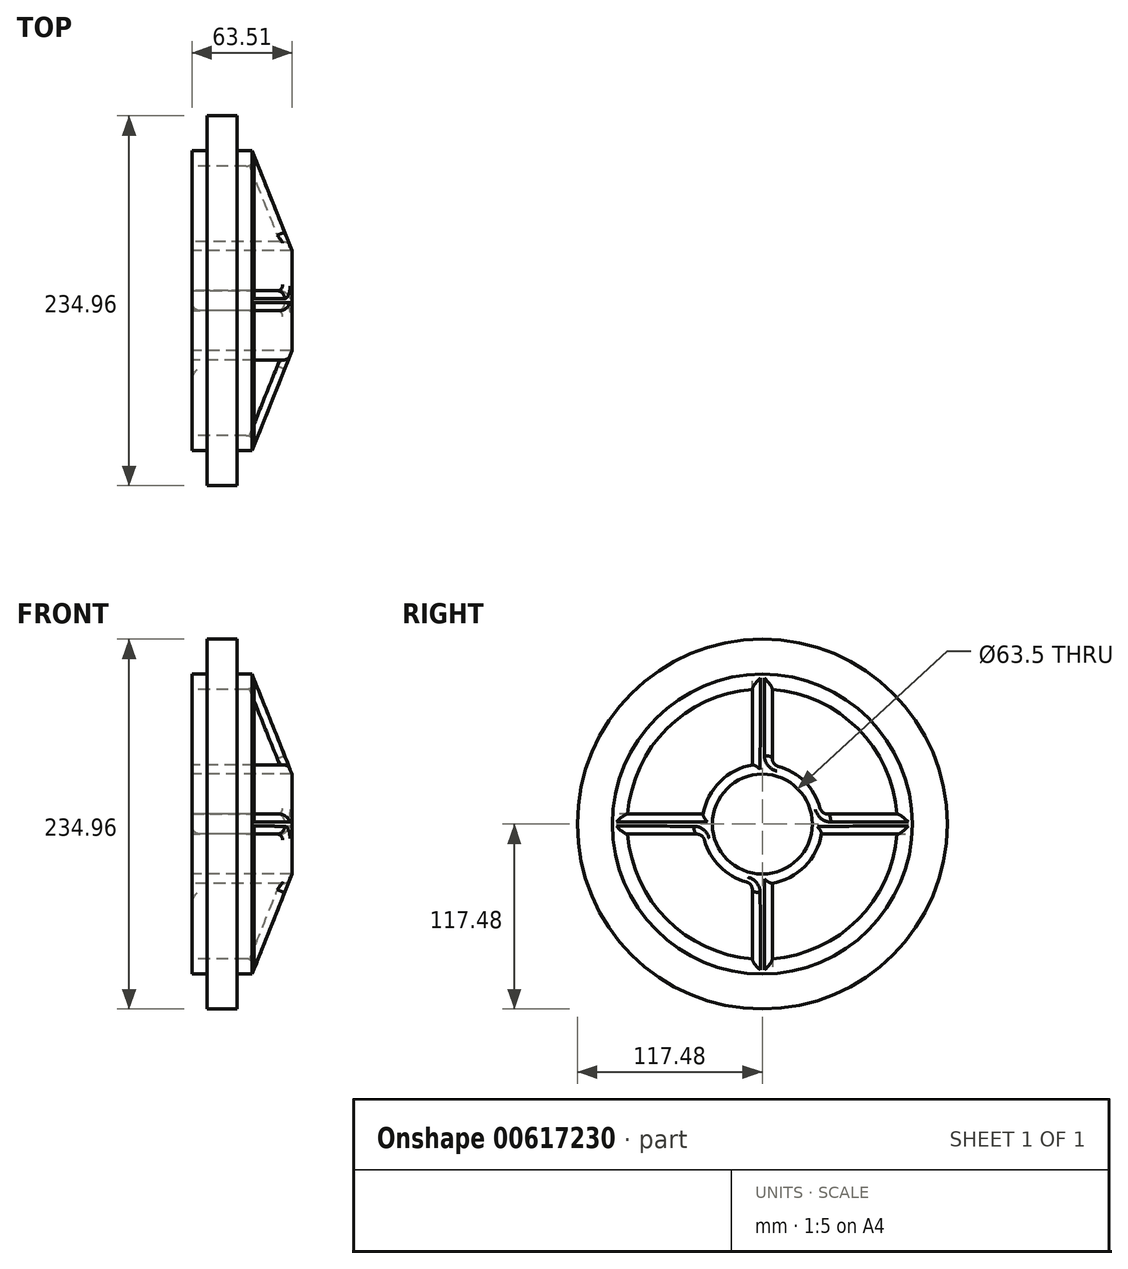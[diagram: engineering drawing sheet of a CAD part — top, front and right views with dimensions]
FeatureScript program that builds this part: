
annotation { "Feature Type Name" : "Feature", "Feature Type Description" : "" }
export const myFeature = defineFeature(function(context is Context, id is Id, definition is map)
    precondition{}
    {
        {
            var Q0;
            Q0=qCreatedBy(makeId("Front.planeOp"),FACE);
            var sketch = newSketch(context, id + "F0", { "sketchPlane" : qUnion([Q0])});
            skLineSegment(sketch, "E0", {"start": v(0, 117.48) * mm, "end": v(19.05, 117.48) * mm});
            skLineSegment(sketch, "E1", {"start": v(19.05, 117.48) * mm, "end": v(19.05, 31.75) * mm});
            skLineSegment(sketch, "E2.bottom", {"start": v(0, 0) * mm, "end": v(0, 0) * mm});
            skLineSegment(sketch, "E2.top", {"start": v(0, 6.04) * mm, "end": v(0, 6.04) * mm});
            skLineSegment(sketch, "E3.top", {"start": v(0, 95.25) * mm, "end": v(-9.53, 95.25) * mm});
            skLineSegment(sketch, "E3.right", {"start": v(-9.52, 31.75) * mm, "end": v(-9.53, 95.25) * mm});
            skLineSegment(sketch, "E4", {"start": v(-9.52, 31.75) * mm, "end": v(53.97, 31.75) * mm});
            skLineSegment(sketch, "E5", {"start": v(19.05, 95.25) * mm, "end": v(28.58, 95.25) * mm});
            skLineSegment(sketch, "E6", {"start": v(-9.53, 31.75) * mm, "end": v(53.97, 31.75) * mm});
            skLineSegment(sketch, "E7", {"start": v(53.97, 31.75) * mm, "end": v(28.57, 95.25) * mm});
            skPoint(sketch, "E8.orphan", {"position": v(19.05, 0) * mm});
            skLineSegment(sketch, "E9.trimOffspring", {"start": v(0, 31.75) * mm, "end": v(0, 95.25) * mm});
            skLineSegment(sketch, "E10.trimOffspring", {"start": v(0, 31.75) * mm, "end": v(0, 117.48) * mm});
            skPoint(sketch, "E11.end.orphan", {"position": v(9.52, 95.25) * mm});
            skPoint(sketch, "E12.start.orphan", {"position": v(-38.35, 0) * mm});
            skLineSegment(sketch, "E13", {"start": v(-18.78, 0) * mm, "end": v(42.61, 0) * mm});
            skSolve(sketch);
        }
        {
            var Q0;
            Q0 = qSketchRegion(id + "F0", true);
            var Q1;
            Q1=sQuery(id+"F0.wireOp",EDGE,"E13");
            revolve(context, id + "F1", {"entities" : qUnion([Q0]), "axis" : qUnion([Q1]), "revolveType" : RevolveType.FULL});
        }
        {
            var Q0;
            Q0=makeQuery(id+"F1.opRevolve","SWEPT_FACE",FACE,{"disambiguationData":[OSD([sQuery(id+"F0.wireOp",EDGE,"E3.right")])]});
            var sketch = newSketch(context, id + "F2", { "sketchPlane" : qUnion([Q0])});
            skLineSegment(sketch, "E14.left", {"start": v(6.35, 85.49) * mm, "end": v(6.35, 37.57) * mm});
            skLineSegment(sketch, "E14.right", {"start": v(-6.35, 85.49) * mm, "end": v(-6.35, 37.57) * mm});
            skLineSegment(sketch, "E15.bottom", {"start": v(85.49, 6.35) * mm, "end": v(37.57, 6.35) * mm});
            skLineSegment(sketch, "E15.top", {"start": v(85.49, -6.35) * mm, "end": v(37.57, -6.35) * mm});
            skArc(sketch, "E16", {"start": v(-6.35, 37.57) * mm, "mid": v(-26.94, 26.94) * mm, "end": v(-37.57, 6.35) * mm});
            skArc(sketch, "E17", {"start": v(-85.49, -6.35) * mm, "mid": v(-60.62, -60.62) * mm, "end": v(-6.35, -85.49) * mm});
            skPoint(sketch, "E18.orphan", {"position": v(-95.04, 6.35) * mm});
            skPoint(sketch, "E19.orphan", {"position": v(-95.04, -6.35) * mm});
            skArc(sketch, "E20.trimOffspring", {"start": v(6.35, -85.49) * mm, "mid": v(60.62, -60.62) * mm, "end": v(85.49, -6.35) * mm});
            skArc(sketch, "E21.trimOffspring", {"start": v(85.49, 6.35) * mm, "mid": v(60.62, 60.62) * mm, "end": v(6.35, 85.49) * mm});
            skPoint(sketch, "E15.left.end.orphan", {"position": v(95.04, -6.35) * mm});
            skPoint(sketch, "E15.left.start.orphan", {"position": v(95.04, 6.35) * mm});
            skPoint(sketch, "E14.top.end.orphan", {"position": v(-6.35, -95.04) * mm});
            skPoint(sketch, "E14.top.start.orphan", {"position": v(6.35, -95.04) * mm});
            skPoint(sketch, "E22.orphan", {"position": v(-6.35, 95.04) * mm});
            skPoint(sketch, "E23.orphan", {"position": v(6.35, 95.04) * mm});
            skArc(sketch, "E24.trimOffspring", {"start": v(-6.35, 85.49) * mm, "mid": v(-60.62, 60.62) * mm, "end": v(-85.49, 6.35) * mm});
            skLineSegment(sketch, "E25.trimOffspring", {"start": v(-37.57, -6.35) * mm, "end": v(-85.49, -6.35) * mm});
            skLineSegment(sketch, "E26.trimOffspring", {"start": v(-37.57, 6.35) * mm, "end": v(-85.49, 6.35) * mm});
            skLineSegment(sketch, "E27.trimOffspring", {"start": v(6.35, -37.57) * mm, "end": v(6.35, -85.49) * mm});
            skLineSegment(sketch, "E28.trimOffspring", {"start": v(-6.35, -37.57) * mm, "end": v(-6.35, -85.49) * mm});
            skArc(sketch, "E29.trimOffspring", {"start": v(-37.57, -6.35) * mm, "mid": v(-26.94, -26.94) * mm, "end": v(-6.35, -37.57) * mm});
            skArc(sketch, "E30.trimOffspring", {"start": v(6.35, -37.57) * mm, "mid": v(26.94, -26.94) * mm, "end": v(37.57, -6.35) * mm});
            skArc(sketch, "E31.trimOffspring", {"start": v(37.57, 6.35) * mm, "mid": v(26.94, 26.94) * mm, "end": v(6.35, 37.57) * mm});
            skSolve(sketch);
        }
        {
            var Q0;
            Q0 = qSketchRegion(id + "F2", true);
            extrude(context, id + "F3", {"entities" : qUnion([Q0]), "operationType" : NewBodyOperationType.REMOVE, "endBound" : BoundingType.THROUGH_ALL, "oppositeDirection" : true, "depth" : 25.4 * mm, "offsetDistance" : 25.4 * mm});
        }
        {
            var Q0;
            Q0=makeQuery(id+"F3.boolean.opBoolean","INTERSECT",EDGE,{"derivedFrom":[makeQuery(id+"F1.opRevolve","SWEPT_FACE",FACE,{"disambiguationData":[OSD([sQuery(id+"F0.wireOp",EDGE,"E7")])]}),makeQuery(id+"F3.opExtrude","SWEPT_FACE",FACE,{"disambiguationData":[OSD([sQuery(id+"F2.wireOp",EDGE,"E15.top")])]})]});
            var Q1;
            Q1=makeQuery(id+"F3.boolean.opBoolean","INTERSECT",EDGE,{"derivedFrom":[makeQuery(id+"F1.opRevolve","SWEPT_FACE",FACE,{"disambiguationData":[OSD([sQuery(id+"F0.wireOp",EDGE,"E7")])]}),makeQuery(id+"F3.opExtrude","SWEPT_FACE",FACE,{"disambiguationData":[OSD([sQuery(id+"F2.wireOp",EDGE,"E15.bottom")])]})]});
            var Q2;
            Q2=makeQuery(id+"F3.boolean.opBoolean","INTERSECT",EDGE,{"derivedFrom":[makeQuery(id+"F1.opRevolve","SWEPT_FACE",FACE,{"disambiguationData":[OSD([sQuery(id+"F0.wireOp",EDGE,"E7")])]}),makeQuery(id+"F3.opExtrude","SWEPT_FACE",FACE,{"disambiguationData":[OSD([sQuery(id+"F2.wireOp",EDGE,"E14.left")])]})]});
            var Q3;
            Q3=makeQuery(id+"F3.boolean.opBoolean","INTERSECT",EDGE,{"derivedFrom":[makeQuery(id+"F1.opRevolve","SWEPT_FACE",FACE,{"disambiguationData":[OSD([sQuery(id+"F0.wireOp",EDGE,"E7")])]}),makeQuery(id+"F3.opExtrude","SWEPT_FACE",FACE,{"disambiguationData":[OSD([sQuery(id+"F2.wireOp",EDGE,"E14.right")])]})]});
            var Q4;
            Q4=makeQuery(id+"F3.boolean.opBoolean","INTERSECT",EDGE,{"derivedFrom":[makeQuery(id+"F1.opRevolve","SWEPT_FACE",FACE,{"disambiguationData":[OSD([sQuery(id+"F0.wireOp",EDGE,"E7")])]}),makeQuery(id+"F3.opExtrude","SWEPT_FACE",FACE,{"disambiguationData":[OSD([sQuery(id+"F2.wireOp",EDGE,"E27.trimOffspring")])]})]});
            var Q5;
            Q5=makeQuery(id+"F3.boolean.opBoolean","INTERSECT",EDGE,{"derivedFrom":[makeQuery(id+"F1.opRevolve","SWEPT_FACE",FACE,{"disambiguationData":[OSD([sQuery(id+"F0.wireOp",EDGE,"E7")])]}),makeQuery(id+"F3.opExtrude","SWEPT_FACE",FACE,{"disambiguationData":[OSD([sQuery(id+"F2.wireOp",EDGE,"E28.trimOffspring")])]})]});
            var Q6;
            Q6=makeQuery(id+"F3.boolean.opBoolean","INTERSECT",EDGE,{"derivedFrom":[makeQuery(id+"F1.opRevolve","SWEPT_FACE",FACE,{"disambiguationData":[OSD([sQuery(id+"F0.wireOp",EDGE,"E7")])]}),makeQuery(id+"F3.opExtrude","SWEPT_FACE",FACE,{"disambiguationData":[OSD([sQuery(id+"F2.wireOp",EDGE,"E25.trimOffspring")])]})]});
            var Q7;
            Q7=makeQuery(id+"F3.boolean.opBoolean","INTERSECT",EDGE,{"derivedFrom":[makeQuery(id+"F1.opRevolve","SWEPT_FACE",FACE,{"disambiguationData":[OSD([sQuery(id+"F0.wireOp",EDGE,"E7")])]}),makeQuery(id+"F3.opExtrude","SWEPT_FACE",FACE,{"disambiguationData":[OSD([sQuery(id+"F2.wireOp",EDGE,"E26.trimOffspring")])]})]});
            var Q8;
            Q8=makeQuery(id+"F3.boolean.opBoolean","INTERSECT",EDGE,{"derivedFrom":[makeQuery(id+"F1.opRevolve","SWEPT_FACE",FACE,{"disambiguationData":[OSD([sQuery(id+"F0.wireOp",EDGE,"E7")])]}),makeQuery(id+"F3.opExtrude","SWEPT_FACE",FACE,{"disambiguationData":[OSD([sQuery(id+"F2.wireOp",EDGE,"E31.trimOffspring")])]})]});
            var Q9;
            Q9=makeQuery(id+"F3.boolean.opBoolean","INTERSECT",EDGE,{"derivedFrom":[makeQuery(id+"F1.opRevolve","SWEPT_FACE",FACE,{"disambiguationData":[OSD([sQuery(id+"F0.wireOp",EDGE,"E7")])]}),makeQuery(id+"F3.opExtrude","SWEPT_FACE",FACE,{"disambiguationData":[OSD([sQuery(id+"F2.wireOp",EDGE,"E30.trimOffspring")])]})]});
            var Q10;
            Q10=makeQuery(id+"F3.boolean.opBoolean","INTERSECT",EDGE,{"derivedFrom":[makeQuery(id+"F1.opRevolve","SWEPT_FACE",FACE,{"disambiguationData":[OSD([sQuery(id+"F0.wireOp",EDGE,"E7")])]}),makeQuery(id+"F3.opExtrude","SWEPT_FACE",FACE,{"disambiguationData":[OSD([sQuery(id+"F2.wireOp",EDGE,"E29.trimOffspring")])]})]});
            var Q11;
            Q11=makeQuery(id+"F3.boolean.opBoolean","INTERSECT",EDGE,{"derivedFrom":[makeQuery(id+"F1.opRevolve","SWEPT_FACE",FACE,{"disambiguationData":[OSD([sQuery(id+"F0.wireOp",EDGE,"E7")])]}),makeQuery(id+"F3.opExtrude","SWEPT_FACE",FACE,{"disambiguationData":[OSD([sQuery(id+"F2.wireOp",EDGE,"E16")])]})]});
            var Q12;
            Q12=makeQuery(id+"F3.boolean.opBoolean","INTERSECT",EDGE,{"derivedFrom":[makeQuery(id+"F1.opRevolve","SWEPT_FACE",FACE,{"disambiguationData":[OSD([sQuery(id+"F0.wireOp",EDGE,"E7")])]}),makeQuery(id+"F3.opExtrude","SWEPT_FACE",FACE,{"disambiguationData":[OSD([sQuery(id+"F2.wireOp",EDGE,"E21.trimOffspring")])]})]});
            var Q13;
            Q13=makeQuery(id+"F3.boolean.opBoolean","INTERSECT",EDGE,{"derivedFrom":[makeQuery(id+"F1.opRevolve","SWEPT_FACE",FACE,{"disambiguationData":[OSD([sQuery(id+"F0.wireOp",EDGE,"E7")])]}),makeQuery(id+"F3.opExtrude","SWEPT_FACE",FACE,{"disambiguationData":[OSD([sQuery(id+"F2.wireOp",EDGE,"E20.trimOffspring")])]})]});
            var Q14;
            Q14=makeQuery(id+"F3.boolean.opBoolean","INTERSECT",EDGE,{"derivedFrom":[makeQuery(id+"F1.opRevolve","SWEPT_FACE",FACE,{"disambiguationData":[OSD([sQuery(id+"F0.wireOp",EDGE,"E7")])]}),makeQuery(id+"F3.opExtrude","SWEPT_FACE",FACE,{"disambiguationData":[OSD([sQuery(id+"F2.wireOp",EDGE,"E17")])]})]});
            var Q15;
            Q15=makeQuery(id+"F3.boolean.opBoolean","INTERSECT",EDGE,{"derivedFrom":[makeQuery(id+"F1.opRevolve","SWEPT_FACE",FACE,{"disambiguationData":[OSD([sQuery(id+"F0.wireOp",EDGE,"E7")])]}),makeQuery(id+"F3.opExtrude","SWEPT_FACE",FACE,{"disambiguationData":[OSD([sQuery(id+"F2.wireOp",EDGE,"E24.trimOffspring")])]})]});
            var Q16;
            Q16=makeQuery(id+"F3.boolean.opBoolean","COPY",EDGE,{"derivedFrom":makeQuery(id+"F3.opExtrude","CAP_EDGE",EDGE,{"disambiguationData":[OSD([sQuery(id+"F2.wireOp",EDGE,"E14.left")])],"isStart":true})});
            var Q17;
            Q17=makeQuery(id+"F3.boolean.opBoolean","COPY",EDGE,{"derivedFrom":makeQuery(id+"F3.opExtrude","CAP_EDGE",EDGE,{"disambiguationData":[OSD([sQuery(id+"F2.wireOp",EDGE,"E14.right")])],"isStart":true})});
            var Q18;
            Q18=makeQuery(id+"F3.boolean.opBoolean","COPY",EDGE,{"derivedFrom":makeQuery(id+"F3.opExtrude","CAP_EDGE",EDGE,{"disambiguationData":[OSD([sQuery(id+"F2.wireOp",EDGE,"E24.trimOffspring")])],"isStart":true})});
            var Q19;
            Q19=makeQuery(id+"F3.boolean.opBoolean","COPY",EDGE,{"derivedFrom":makeQuery(id+"F3.opExtrude","CAP_EDGE",EDGE,{"disambiguationData":[OSD([sQuery(id+"F2.wireOp",EDGE,"E26.trimOffspring")])],"isStart":true})});
            var Q20;
            Q20=makeQuery(id+"F3.boolean.opBoolean","COPY",EDGE,{"derivedFrom":makeQuery(id+"F3.opExtrude","CAP_EDGE",EDGE,{"disambiguationData":[OSD([sQuery(id+"F2.wireOp",EDGE,"E16")])],"isStart":true})});
            var Q21;
            Q21=makeQuery(id+"F3.boolean.opBoolean","COPY",EDGE,{"derivedFrom":makeQuery(id+"F3.opExtrude","CAP_EDGE",EDGE,{"disambiguationData":[OSD([sQuery(id+"F2.wireOp",EDGE,"E25.trimOffspring")])],"isStart":true})});
            var Q22;
            Q22=makeQuery(id+"F3.boolean.opBoolean","COPY",EDGE,{"derivedFrom":makeQuery(id+"F3.opExtrude","CAP_EDGE",EDGE,{"disambiguationData":[OSD([sQuery(id+"F2.wireOp",EDGE,"E17")])],"isStart":true})});
            var Q23;
            Q23=makeQuery(id+"F3.boolean.opBoolean","COPY",EDGE,{"derivedFrom":makeQuery(id+"F3.opExtrude","CAP_EDGE",EDGE,{"disambiguationData":[OSD([sQuery(id+"F2.wireOp",EDGE,"E29.trimOffspring")])],"isStart":true})});
            var Q24;
            Q24=makeQuery(id+"F3.boolean.opBoolean","COPY",EDGE,{"derivedFrom":makeQuery(id+"F3.opExtrude","CAP_EDGE",EDGE,{"disambiguationData":[OSD([sQuery(id+"F2.wireOp",EDGE,"E28.trimOffspring")])],"isStart":true})});
            var Q25;
            Q25=makeQuery(id+"F3.boolean.opBoolean","COPY",EDGE,{"derivedFrom":makeQuery(id+"F3.opExtrude","CAP_EDGE",EDGE,{"disambiguationData":[OSD([sQuery(id+"F2.wireOp",EDGE,"E27.trimOffspring")])],"isStart":true})});
            var Q26;
            Q26=makeQuery(id+"F3.boolean.opBoolean","COPY",EDGE,{"derivedFrom":makeQuery(id+"F3.opExtrude","CAP_EDGE",EDGE,{"disambiguationData":[OSD([sQuery(id+"F2.wireOp",EDGE,"E20.trimOffspring")])],"isStart":true})});
            var Q27;
            Q27=makeQuery(id+"F3.boolean.opBoolean","COPY",EDGE,{"derivedFrom":makeQuery(id+"F3.opExtrude","CAP_EDGE",EDGE,{"disambiguationData":[OSD([sQuery(id+"F2.wireOp",EDGE,"E15.top")])],"isStart":true})});
            var Q28;
            Q28=makeQuery(id+"F3.boolean.opBoolean","COPY",EDGE,{"derivedFrom":makeQuery(id+"F3.opExtrude","CAP_EDGE",EDGE,{"disambiguationData":[OSD([sQuery(id+"F2.wireOp",EDGE,"E30.trimOffspring")])],"isStart":true})});
            var Q29;
            Q29=makeQuery(id+"F3.boolean.opBoolean","COPY",EDGE,{"derivedFrom":makeQuery(id+"F3.opExtrude","CAP_EDGE",EDGE,{"disambiguationData":[OSD([sQuery(id+"F2.wireOp",EDGE,"E15.bottom")])],"isStart":true})});
            var Q30;
            Q30=makeQuery(id+"F3.boolean.opBoolean","COPY",EDGE,{"derivedFrom":makeQuery(id+"F3.opExtrude","CAP_EDGE",EDGE,{"disambiguationData":[OSD([sQuery(id+"F2.wireOp",EDGE,"E21.trimOffspring")])],"isStart":true})});
            var Q31;
            Q31=makeQuery(id+"F3.boolean.opBoolean","COPY",EDGE,{"derivedFrom":makeQuery(id+"F3.opExtrude","CAP_EDGE",EDGE,{"disambiguationData":[OSD([sQuery(id+"F2.wireOp",EDGE,"E31.trimOffspring")])],"isStart":true})});
            var Q32;
            Q32=makeQuery(id+"F3.boolean.opBoolean","COPY",EDGE,{"derivedFrom":makeQuery(id+"F3.opExtrude","SWEPT_EDGE",EDGE,{"disambiguationData":[OSD([sQuery(id+"F2.wireOp",EDGE,"E15.top"),sQuery(id+"F2.wireOp",EDGE,"E30.trimOffspring")])]})});
            var Q33;
            Q33=makeQuery(id+"F3.boolean.opBoolean","COPY",FACE,{"derivedFrom":makeQuery(id+"F3.opExtrude","SWEPT_FACE",FACE,{"disambiguationData":[OSD([sQuery(id+"F2.wireOp",EDGE,"E30.trimOffspring")])]})});
            var Q34;
            Q34=makeQuery(id+"F3.boolean.opBoolean","COPY",EDGE,{"derivedFrom":makeQuery(id+"F3.opExtrude","SWEPT_EDGE",EDGE,{"disambiguationData":[OSD([sQuery(id+"F2.wireOp",EDGE,"E16"),sQuery(id+"F2.wireOp",EDGE,"E26.trimOffspring")])]})});
            var Q35;
            Q35=makeQuery(id+"F3.boolean.opBoolean","COPY",EDGE,{"derivedFrom":makeQuery(id+"F3.opExtrude","SWEPT_EDGE",EDGE,{"disambiguationData":[OSD([sQuery(id+"F2.wireOp",EDGE,"E14.right"),sQuery(id+"F2.wireOp",EDGE,"E16")])]})});
            fillet(context, id + "F4", {"entities" : qUnion([Q0, Q1, Q2, Q3, Q4, Q5, Q6, Q7, Q8, Q9, Q10, Q11, Q12, Q13, Q14, Q15, Q16, Q17, Q18, Q19, Q20, Q21, Q22, Q23, Q24, Q25, Q26, Q27, Q28, Q29, Q30, Q31, Q32, Q33, Q34, Q35]), "radius" : 5.08 * mm, "tangentPropagation" : true, "allowEdgeOverflow" : false});
        }
    });
